# Revit family: GIU_v_1.01
name_source: partatom
category: Окна
revit_build: Autodesk Revit 2017 (Build: 20160225_1515(x64)
units: mm (PartAtom-declared; Revit-internal decimal feet)

## family parameters
Всегда вертикально = Нет
Общий = Нет
Основа = Крыша
При загрузке вырезать с полостями = Нет
Точка расчета площади = Нет

## types (1)
- PK34
    Allowed Roof Slope = 15°-90°
    Date of publishing = 6/27/2013
    Design country = Denmark
    Edition number = 1
    Emergency Exit = Нет
    Frame Area = 0.3
    Function = Fixed roof window
    GlazingAreaFraction = 0.56
    IFC Classification = Window
    Installation instructions = http://www.velux.co.uk
    Light transmittance = 0.75
    Manufacturer URL = www.velux.com
    Manufacturer country = Denmark
    Material main = Wood
    Material secondary = Glass 73Q + ISD 0000
    NBS Reference = 59-72
    NBS Reference Description = Roof Window Units
    Name of the object = New Generation - GIU
    Operation Mode = Fixed
    Perimeter Glazing = 2.97
    Perimeter Window = 3.72
    Placement Height = 0 мм
    Product SKU = giu101
    Product data url = http://www.velux.co.uk
    Product family = Fixed window
    Product group = GIU 1.01
    Roof Slope = 45.00°
    Sound Insulation db = 35
    Square Reveal Length = 150 мм
    Thermal Transmittance(frame) = 1.3
    Thermal bridge = 0.09
    Thermal bridge(glazing) = 0.059
    ThermalTransmittance = 1.3
    ThermalTransmittance - Glazing = 1.0
    UNSPC Category = Roofing accessories
    UNSPC code = 301516
    URL = http://file-system.ru
    Uniclass 1.4 Code = JL11
    Uniclass 1.4 Description = Rooflights/Roof windows
    Uniclass 2.0 Code = PR-59-72
    Uniclass 2.0 Description = Roof Window Units
    Warranty Years = 5 (10 with BDX)
    Window Area = 0.86
    g-value = 0.52
    Высота = 920 мм
    Группа модели = New Generation - GIU
    Изготовитель = VELUX A/S
    Код по классификатору = B3020110
    Ширина = 940 мм

## geometry (parser evidence)
native form markers: Blend x56, Sweep x2
no freeform markers — native parametric forms only
